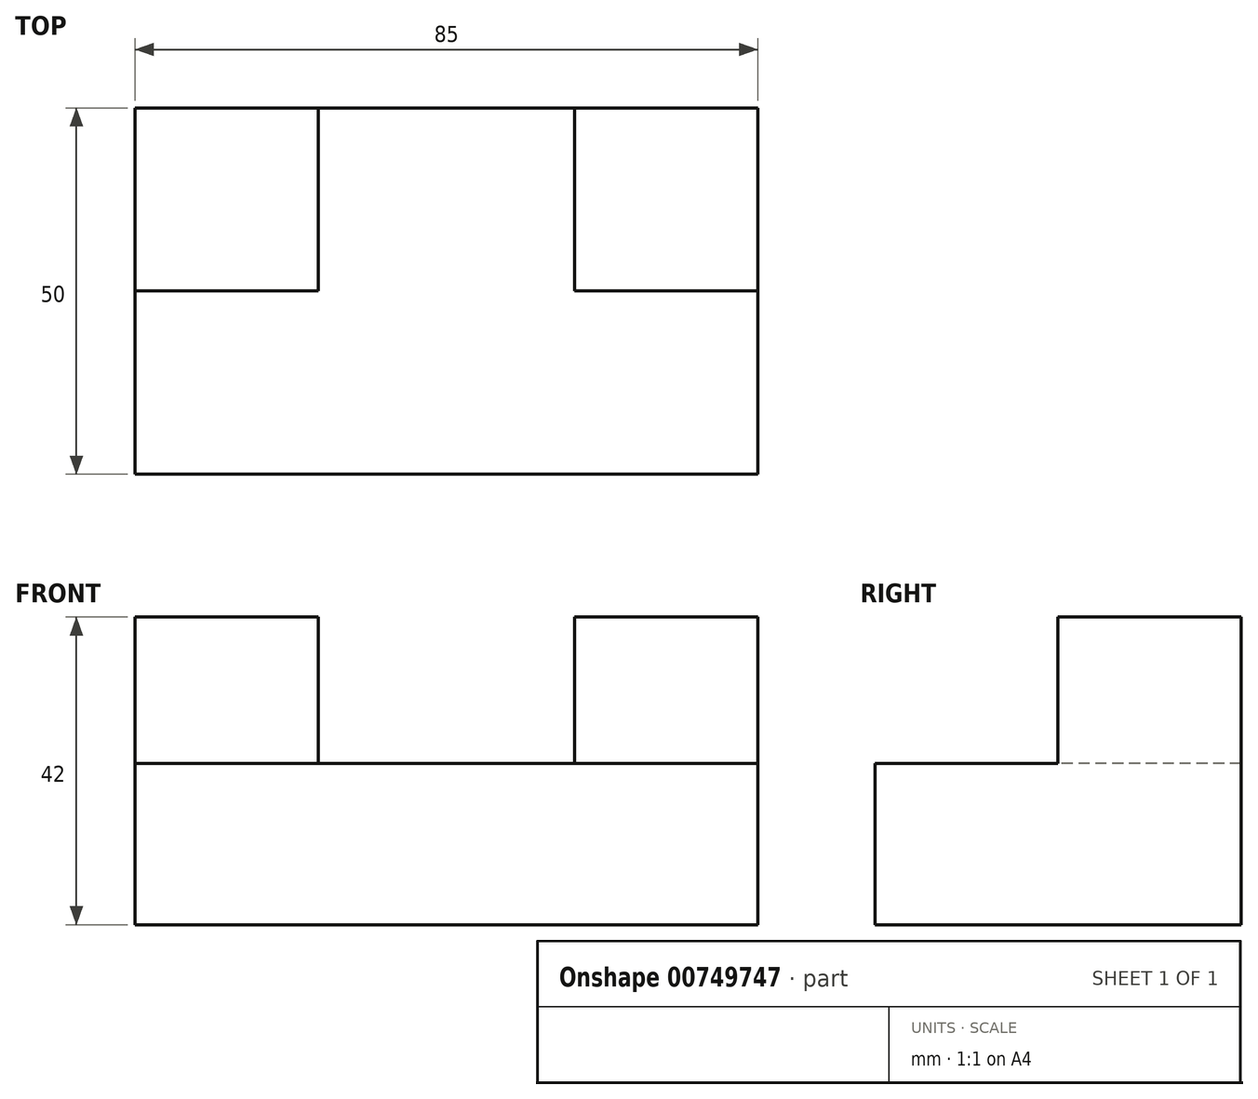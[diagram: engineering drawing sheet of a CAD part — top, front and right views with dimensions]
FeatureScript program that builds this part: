
annotation { "Feature Type Name" : "Feature", "Feature Type Description" : "" }
export const myFeature = defineFeature(function(context is Context, id is Id, definition is map)
    precondition{}
    {
        {
            var Q0;
            Q0=qCreatedBy(makeId("Top.planeOp"),FACE);
            var sketch = newSketch(context, id + "F0", { "sketchPlane" : qUnion([Q0])});
            skLineSegment(sketch, "E0.bottom", {"start": v(0, 0) * mm, "end": v(85, 0) * mm});
            skLineSegment(sketch, "E0.top", {"start": v(0, 50) * mm, "end": v(85, 50) * mm});
            skLineSegment(sketch, "E0.left", {"start": v(0, 0) * mm, "end": v(0, 50) * mm});
            skLineSegment(sketch, "E0.right", {"start": v(85, 0) * mm, "end": v(85, 50) * mm});
            skLineSegment(sketch, "E1.bottom", {"start": v(0, 50) * mm, "end": v(25, 50) * mm});
            skLineSegment(sketch, "E1.top", {"start": v(0, 25) * mm, "end": v(25, 25) * mm});
            skLineSegment(sketch, "E1.left", {"start": v(0, 50) * mm, "end": v(0, 25) * mm});
            skLineSegment(sketch, "E1.right", {"start": v(25, 50) * mm, "end": v(25, 25) * mm});
            skLineSegment(sketch, "E2.bottom", {"start": v(85, 50) * mm, "end": v(60, 50) * mm});
            skLineSegment(sketch, "E2.top", {"start": v(85, 25) * mm, "end": v(60, 25) * mm});
            skLineSegment(sketch, "E2.left", {"start": v(85, 50) * mm, "end": v(85, 25) * mm});
            skLineSegment(sketch, "E2.right", {"start": v(60, 50) * mm, "end": v(60, 25) * mm});
            skSolve(sketch);
        }
        {
            var Q0;
            {var subQ1=sQuery(id+"F0.wireOp",EDGE,"E0.bottom");Q0=makeQuery(id+"F0.imprint","IMPRINT",FACE,{"disambiguationData":[TD([[makeQuery(id+"F0.imprint","IMPRINT",EDGE,{"derivedFrom":subQ1}),1.0]])]});}
            extrude(context, id + "F1", {"entities" : qUnion([Q0]), "depth" : 22 * mm, "offsetDistance" : 25 * mm});
        }
        {
            var Q0;
            {var subQ4=sQuery(id+"F0.wireOp",EDGE,"E1.top");Q0=makeQuery(id+"F0.imprint","IMPRINT",FACE,{"disambiguationData":[TD([[makeQuery(id+"F0.imprint","IMPRINT",EDGE,{"derivedFrom":subQ4}),1.0]])]});}
            var Q1;
            {var subQ4=sQuery(id+"F0.wireOp",EDGE,"E2.top");Q1=makeQuery(id+"F0.imprint","IMPRINT",FACE,{"disambiguationData":[TD([[makeQuery(id+"F0.imprint","IMPRINT",EDGE,{"derivedFrom":subQ4}),-1.0]])]});}
            extrude(context, id + "F2", {"entities" : qUnion([Q0, Q1]), "operationType" : NewBodyOperationType.ADD, "depth" : 42 * mm, "offsetDistance" : 25 * mm});
        }
    });
